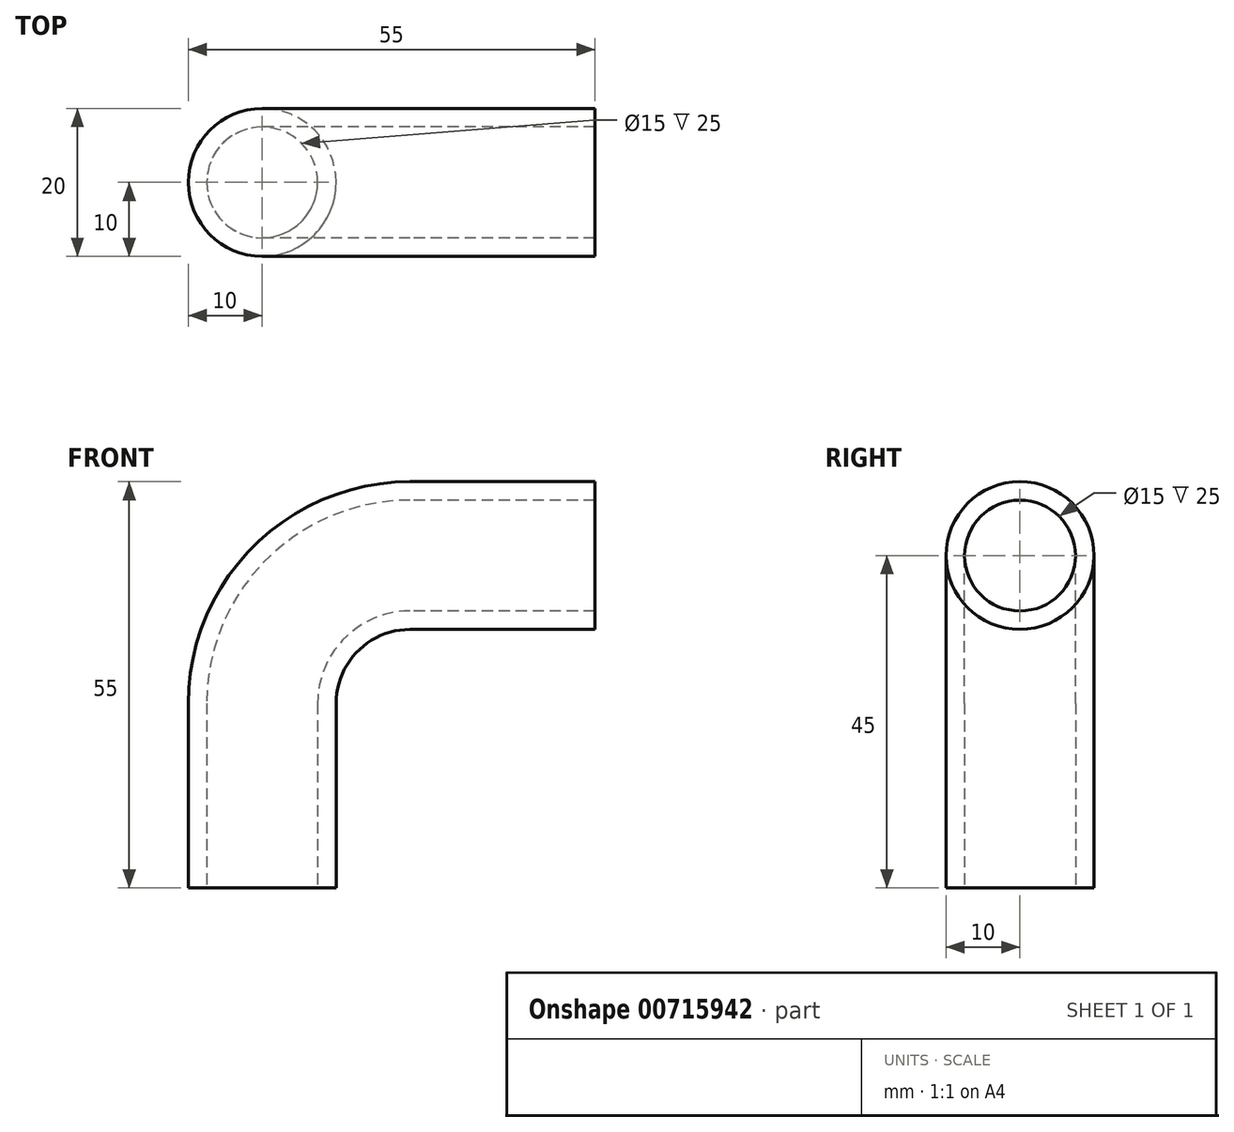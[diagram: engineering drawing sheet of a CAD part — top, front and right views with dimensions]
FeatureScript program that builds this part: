
annotation { "Feature Type Name" : "Feature", "Feature Type Description" : "" }
export const myFeature = defineFeature(function(context is Context, id is Id, definition is map)
    precondition{}
    {
        {
            var Q0;
            Q0=qCreatedBy(makeId("Top.planeOp"),FACE);
            var sketch = newSketch(context, id + "F0", { "sketchPlane" : qUnion([Q0])});
            skCircle(sketch, "E0", {"center": v(0, 0) * mm, "radius": 10 * mm});
            skCircle(sketch, "E1", {"center": v(0, 0) * mm, "radius": 7.5 * mm});
            skSolve(sketch);
        }
        {
            var Q0;
            Q0=makeQuery(id+"F0.imprint","IMPRINT",FACE,{"disambiguationData":[TD([[makeQuery(id+"F0.imprint","IMPRINT",EDGE,{"derivedFrom":sQuery(id+"F0.wireOp",EDGE,"E0")}),1.0]])]});
            extrude(context, id + "F1", {"entities" : qUnion([Q0]), "depth" : 25 * mm, "offsetDistance" : 25 * mm});
        }
        {
            var Q0;
            Q0=qCreatedBy(makeId("Front.planeOp"),FACE);
            var sketch = newSketch(context, id + "F2", { "sketchPlane" : qUnion([Q0])});
            skLineSegment(sketch, "E2", {"start": v(0, 25) * mm, "end": v(0, 0) * mm, "construction": true});
            skLineSegment(sketch, "E3", {"start": v(20, 25) * mm, "end": v(0, 25) * mm, "construction": true});
            skLineSegment(sketch, "E4", {"start": v(20, 25) * mm, "end": v(20, 35) * mm, "construction": true});
            skLineSegment(sketch, "E5", {"start": v(20, 35) * mm, "end": v(45, 35) * mm, "construction": true});
            skSolve(sketch);
        }
        {
            var Q0;
            Q0=makeQuery(id+"F1.opExtrude","CAP_FACE",FACE,{"disambiguationData":[OSD([sQuery(id+"F0.wireOp",EDGE,"E0"),sQuery(id+"F0.wireOp",EDGE,"E1")])],"isStart":false});
            var sketch = newSketch(context, id + "F3", { "sketchPlane" : qUnion([Q0])});
            skLineSegment(sketch, "E6", {"start": v(20, 10) * mm, "end": v(20, -10) * mm, "construction": true});
            skSolve(sketch);
        }
        {
            var Q0;
            Q0=makeQuery(id+"F3.imprint","IMPRINT",FACE,{"disambiguationData":[TD([[makeQuery(id+"F3.imprint","IMPRINT",EDGE,{"derivedFrom":makeQuery(id+"F1.opExtrude","CAP_EDGE",EDGE,{"disambiguationData":[OSD([sQuery(id+"F0.wireOp",EDGE,"E0")])],"isStart":false})}),1.0]])]});
            var Q1;
            Q1=sQuery(id+"F3.wireOp",EDGE,"E6");
            revolve(context, id + "F4", {"operationType" : NewBodyOperationType.ADD, "surfaceOperationType" : NewSurfaceOperationType.NEW, "entities" : qUnion([Q0]), "axis" : qUnion([Q1]), "revolveType" : RevolveType.ONE_DIRECTION, "oppositeDirection" : true, "angle" : 90 * degree});
        }
        {
            var Q0;
            Q0=makeQuery(id+"F4.opRevolve","CAP_FACE",FACE,{"disambiguationData":[OSD([sQuery(id+"F0.wireOp",EDGE,"E0"),sQuery(id+"F0.wireOp",EDGE,"E1")])],"isStart":false});
            extrude(context, id + "F5", {"entities" : qUnion([Q0]), "operationType" : NewBodyOperationType.ADD, "depth" : 25 * mm, "offsetDistance" : 25 * mm});
        }
    });
